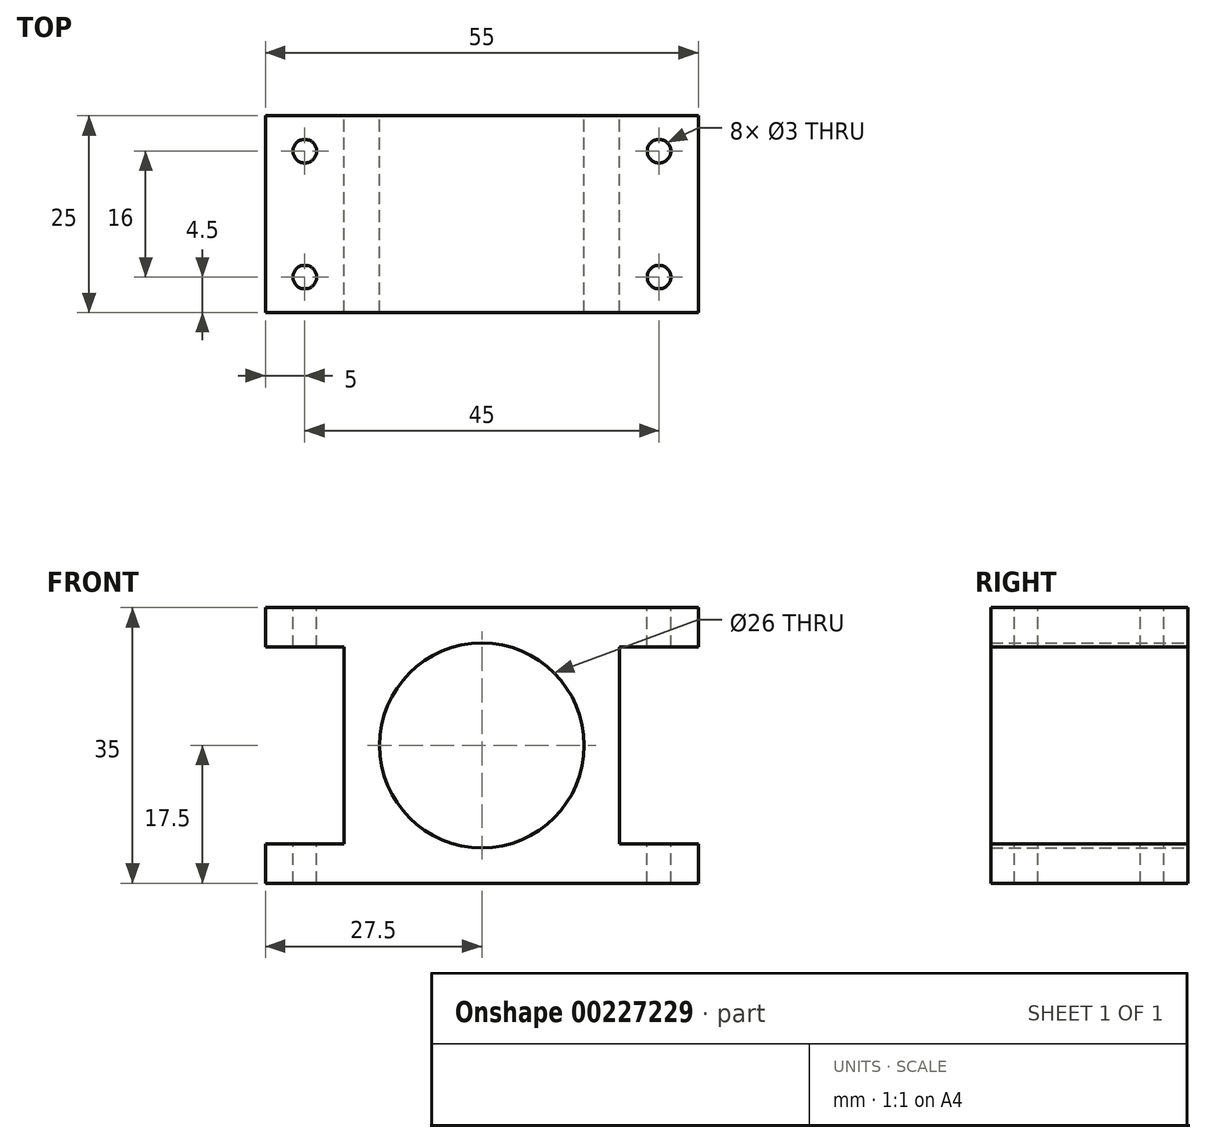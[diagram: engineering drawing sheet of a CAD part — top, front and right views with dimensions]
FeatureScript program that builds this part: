
annotation { "Feature Type Name" : "Feature", "Feature Type Description" : "" }
export const myFeature = defineFeature(function(context is Context, id is Id, definition is map)
    precondition{}
    {
        {
            var Q0;
            Q0=qCreatedBy(makeId("Front.planeOp"),FACE);
            var sketch = newSketch(context, id + "F0", { "sketchPlane" : qUnion([Q0])});
            skCircle(sketch, "E0", {"center": v(0, 0) * mm, "radius": 13 * mm});
            skLineSegment(sketch, "E1.bottom", {"start": v(17.5, -17.5) * mm, "end": v(-17.5, -17.5) * mm});
            skLineSegment(sketch, "E1.top", {"start": v(17.5, 17.5) * mm, "end": v(-17.5, 17.5) * mm});
            skLineSegment(sketch, "E1.left", {"start": v(17.5, -17.5) * mm, "end": v(17.5, 17.5) * mm});
            skLineSegment(sketch, "E1.right", {"start": v(-17.5, -17.5) * mm, "end": v(-17.5, 17.5) * mm});
            skLineSegment(sketch, "E2", {"start": v(-17.5, 17.5) * mm, "end": v(-27.5, 17.5) * mm});
            skLineSegment(sketch, "E3", {"start": v(-27.5, 17.5) * mm, "end": v(-27.5, 12.5) * mm});
            skLineSegment(sketch, "E4", {"start": v(-27.5, -17.5) * mm, "end": v(-17.5, -17.5) * mm});
            skLineSegment(sketch, "E5", {"start": v(-27.5, 12.5) * mm, "end": v(-17.5, 12.5) * mm});
            skLineSegment(sketch, "E6.MirrorCS", {"start": v(-27.5, -12.5) * mm, "end": v(-17.5, -12.5) * mm});
            skLineSegment(sketch, "E7.MirrorCS", {"start": v(27.5, 12.5) * mm, "end": v(17.5, 12.5) * mm});
            skLineSegment(sketch, "E8.MirrorCS", {"start": v(27.5, 17.5) * mm, "end": v(27.5, 12.5) * mm});
            skLineSegment(sketch, "E9.MirrorCS", {"start": v(17.5, 17.5) * mm, "end": v(27.5, 17.5) * mm});
            skLineSegment(sketch, "E10.MirrorCS", {"start": v(27.5, -12.5) * mm, "end": v(17.5, -12.5) * mm});
            skLineSegment(sketch, "E11.MirrorCS", {"start": v(27.5, -17.5) * mm, "end": v(17.5, -17.5) * mm});
            skLineSegment(sketch, "E12.trimOffspring", {"start": v(-27.5, -12.5) * mm, "end": v(-27.5, -17.5) * mm});
            skLineSegment(sketch, "E13.trimOffspring", {"start": v(27.5, -12.5) * mm, "end": v(27.5, -17.5) * mm});
            skSolve(sketch);
        }
        {
            var Q0;
            Q0 = qSketchRegion(id + "F0", true);
            extrude(context, id + "F1", {"entities" : qUnion([Q0]), "endBound" : BoundingType.SYMMETRIC, "depth" : 25 * mm});
        }
        {
            var Q0;
            Q0=makeQuery(id+"F1.opExtrude","SWEPT_FACE",FACE,{"disambiguationData":[OSD([sQuery(id+"F0.wireOp",EDGE,"E1.top"),sQuery(id+"F0.wireOp",EDGE,"E2"),sQuery(id+"F0.wireOp",EDGE,"E9.MirrorCS")])]});
            var sketch = newSketch(context, id + "F2", { "sketchPlane" : qUnion([Q0])});
            skCircle(sketch, "E14", {"center": v(-22.5, -8) * mm, "radius": 1.5 * mm});
            skCircle(sketch, "E15.MirrorC", {"center": v(-22.5, 8) * mm, "radius": 1.5 * mm});
            skCircle(sketch, "E16.MirrorC", {"center": v(22.5, 8) * mm, "radius": 1.5 * mm});
            skCircle(sketch, "E17.MirrorC", {"center": v(22.5, -8) * mm, "radius": 1.5 * mm});
            skSolve(sketch);
        }
        {
            var Q0;
            Q0 = qSketchRegion(id + "F2", true);
            extrude(context, id + "F3", {"entities" : qUnion([Q0]), "operationType" : NewBodyOperationType.REMOVE, "oppositeDirection" : true, "depth" : 45.1 * mm});
        }
    });
